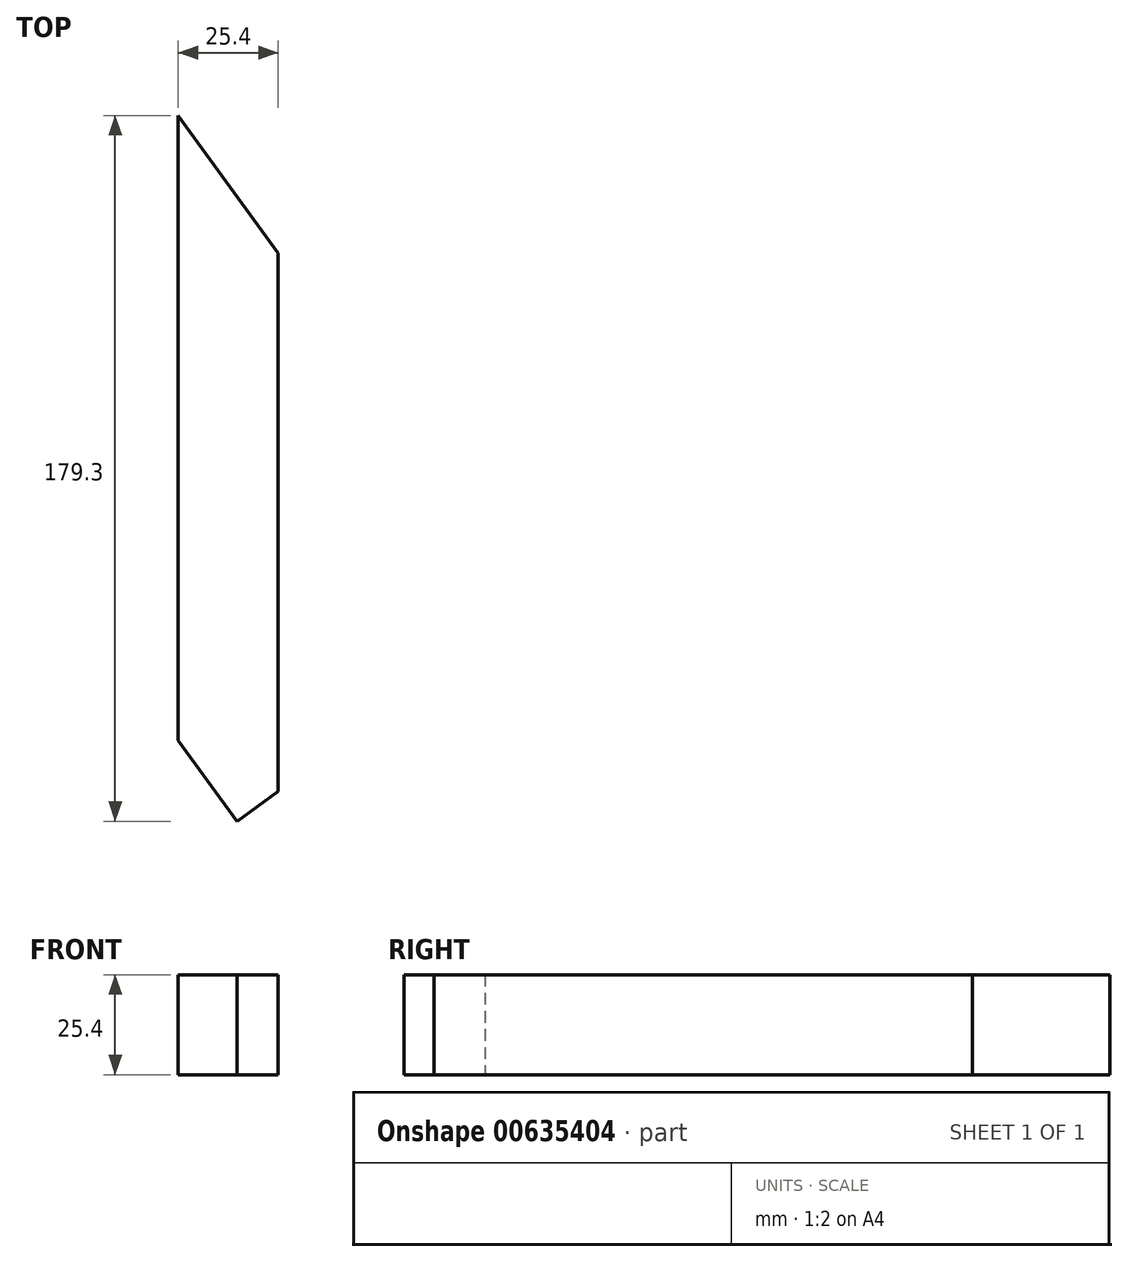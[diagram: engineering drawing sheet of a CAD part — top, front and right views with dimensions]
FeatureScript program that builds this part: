
annotation { "Feature Type Name" : "Feature", "Feature Type Description" : "" }
export const myFeature = defineFeature(function(context is Context, id is Id, definition is map)
    precondition{}
    {
        {
            var Q0;
            Q0=qCreatedBy(makeId("Top.planeOp"),FACE);
            var sketch = newSketch(context, id + "F0", { "sketchPlane" : qUnion([Q0])});
            skLineSegment(sketch, "E0.bottom", {"start": v(-12.7, 89.65) * mm, "end": v(12.7, 89.65) * mm});
            skLineSegment(sketch, "E0.top", {"start": v(-12.7, -89.65) * mm, "end": v(12.7, -89.65) * mm});
            skLineSegment(sketch, "E0.left", {"start": v(-12.7, 89.65) * mm, "end": v(-12.7, -89.65) * mm});
            skLineSegment(sketch, "E0.right", {"start": v(12.7, 89.65) * mm, "end": v(12.7, -89.65) * mm});
            skPoint(sketch, "E0.middle", {"position": v(0, 0) * mm});
            skLineSegment(sketch, "E1", {"start": v(-12.7, -69.1) * mm, "end": v(2.23, -89.65) * mm});
            skLineSegment(sketch, "E2", {"start": v(-12.7, 89.65) * mm, "end": v(12.7, 54.69) * mm});
            skLineSegment(sketch, "E3", {"start": v(2.23, -89.65) * mm, "end": v(12.7, -82.04) * mm});
            skSolve(sketch);
        }
        {
            var Q0;
            {var subQ3=sQuery(id+"F0.wireOp",EDGE,"E1");Q0=makeQuery(id+"F0.imprint","IMPRINT",FACE,{"disambiguationData":[TD([[makeQuery(id+"F0.imprint","IMPRINT",EDGE,{"derivedFrom":subQ3}),1.0]])]});}
            extrude(context, id + "F1", {"entities" : qUnion([Q0]), "depth" : 25.4 * mm});
        }
    });
